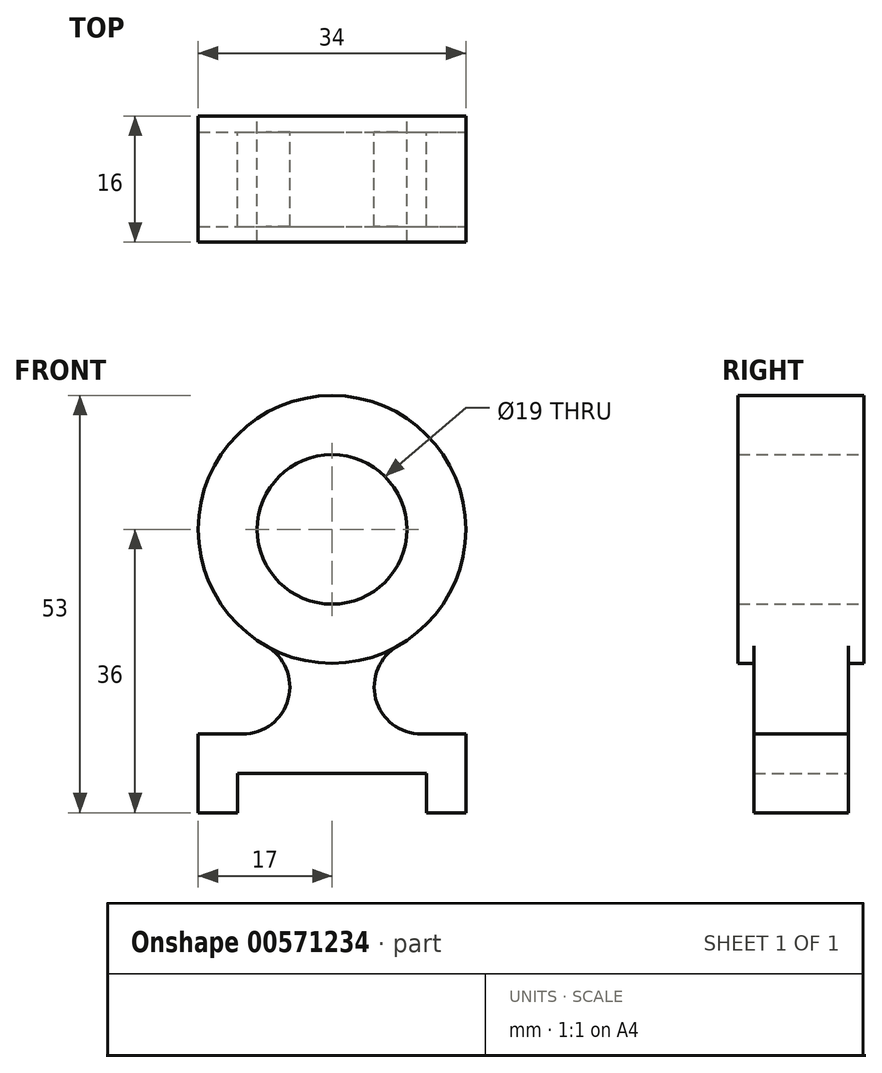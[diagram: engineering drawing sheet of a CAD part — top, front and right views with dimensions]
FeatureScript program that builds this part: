
annotation { "Feature Type Name" : "Feature", "Feature Type Description" : "" }
export const myFeature = defineFeature(function(context is Context, id is Id, definition is map)
    precondition{}
    {
        {
            var Q0;
            Q0=qCreatedBy(makeId("Front.planeOp"),FACE);
            var sketch = newSketch(context, id + "F0", { "sketchPlane" : qUnion([Q0])});
            skCircle(sketch, "E0", {"center": v(0, 0) * mm, "radius": 9.5 * mm});
            skCircle(sketch, "E1", {"center": v(0, 0) * mm, "radius": 17 * mm});
            skLineSegment(sketch, "E2", {"start": v(0, 0) * mm, "end": v(0, -36) * mm, "construction": true});
            skLineSegment(sketch, "E3.bottom", {"start": v(-17, -26) * mm, "end": v(-11.36, -26) * mm});
            skLineSegment(sketch, "E3.top", {"start": v(-17, -36) * mm, "end": v(-12, -36) * mm});
            skLineSegment(sketch, "E3.left", {"start": v(-17, -26) * mm, "end": v(-17, -36) * mm});
            skLineSegment(sketch, "E3.right", {"start": v(17, -26) * mm, "end": v(17, -36) * mm});
            skArc(sketch, "E4", {"start": v(-11.36, -26) * mm, "mid": v(-5.56, -21.53) * mm, "end": v(-8.4, -14.78) * mm});
            skArc(sketch, "E5.MirrorC", {"start": v(11.36, -26) * mm, "mid": v(5.56, -21.53) * mm, "end": v(8.4, -14.78) * mm});
            skLineSegment(sketch, "E6.trimOffspring", {"start": v(11.36, -26) * mm, "end": v(17, -26) * mm});
            skLineSegment(sketch, "E7.bottom", {"start": v(-12, -31) * mm, "end": v(12, -31) * mm});
            skLineSegment(sketch, "E7.left", {"start": v(-12, -31) * mm, "end": v(-12, -36) * mm});
            skLineSegment(sketch, "E7.right", {"start": v(12, -31) * mm, "end": v(12, -36) * mm});
            skLineSegment(sketch, "E8.trimOffspring", {"start": v(12, -36) * mm, "end": v(17, -36) * mm});
            skSolve(sketch);
        }
        {
            var Q0;
            Q0=makeQuery(id+"F0.imprint","IMPRINT",FACE,{"disambiguationData":[TD([[makeQuery(id+"F0.imprint","IMPRINT",EDGE,{"derivedFrom":sQuery(id+"F0.wireOp",EDGE,"E3.bottom")}),-1.0]])]});
            extrude(context, id + "F1", {"entities" : qUnion([Q0]), "endBound" : BoundingType.SYMMETRIC, "depth" : 12 * mm, "offsetDistance" : 25 * mm});
        }
        {
            var Q0;
            Q0=makeQuery(id+"F0.imprint","IMPRINT",FACE,{"disambiguationData":[TD([[makeQuery(id+"F0.imprint","IMPRINT",EDGE,{"derivedFrom":sQuery(id+"F0.wireOp",EDGE,"E0")}),-1.0]])]});
            extrude(context, id + "F2", {"entities" : qUnion([Q0]), "operationType" : NewBodyOperationType.ADD, "endBound" : BoundingType.SYMMETRIC, "depth" : 16 * mm, "offsetDistance" : 25 * mm});
        }
    });
